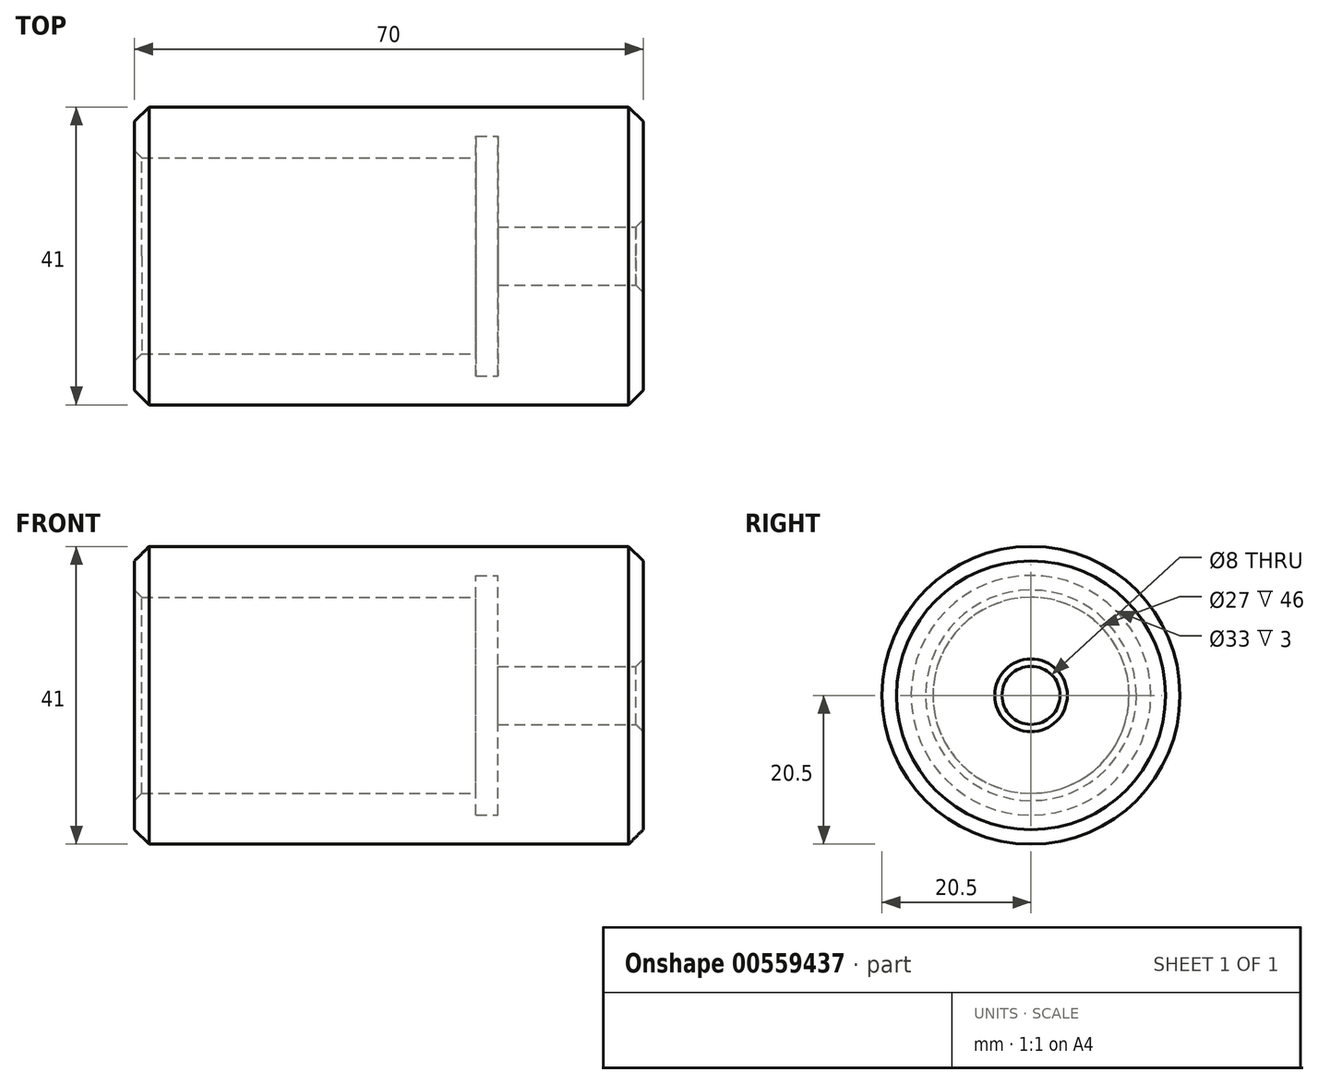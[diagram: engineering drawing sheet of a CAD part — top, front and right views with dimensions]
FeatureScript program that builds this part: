
annotation { "Feature Type Name" : "Feature", "Feature Type Description" : "" }
export const myFeature = defineFeature(function(context is Context, id is Id, definition is map)
    precondition{}
    {
        {
            var Q0;
            Q0=qCreatedBy(makeId("Front.planeOp"),FACE);
            var sketch = newSketch(context, id + "F0", { "sketchPlane" : qUnion([Q0])});
            skLineSegment(sketch, "E0", {"start": v(0, 4) * mm, "end": v(20, 4) * mm});
            skLineSegment(sketch, "E1", {"start": v(20, 4) * mm, "end": v(20, 20.5) * mm});
            skLineSegment(sketch, "E2", {"start": v(20, 20.5) * mm, "end": v(-50, 20.5) * mm});
            skLineSegment(sketch, "E3", {"start": v(-50, 20.5) * mm, "end": v(-50, 13.5) * mm});
            skLineSegment(sketch, "E4", {"start": v(-3, 13.5) * mm, "end": v(-50, 13.5) * mm});
            skLineSegment(sketch, "E5", {"start": v(0, 13.5) * mm, "end": v(0, 4) * mm});
            skPoint(sketch, "E6.start.orphan", {"position": v(-50, 0) * mm});
            skLineSegment(sketch, "E7", {"start": v(21.85, 0) * mm, "end": v(-52.14, 0) * mm, "construction": true});
            skLineSegment(sketch, "E8", {"start": v(-3, -1.98) * mm, "end": v(-3, 15.28) * mm, "construction": true});
            skLineSegment(sketch, "E9", {"start": v(-5.32, 16.5) * mm, "end": v(2.8, 16.5) * mm, "construction": true});
            skLineSegment(sketch, "E10", {"start": v(-3, 13.5) * mm, "end": v(-3, 16.5) * mm});
            skLineSegment(sketch, "E11", {"start": v(-3, 16.5) * mm, "end": v(0, 16.5) * mm});
            skLineSegment(sketch, "E12", {"start": v(0, 16.5) * mm, "end": v(0, 13.5) * mm});
            skSolve(sketch);
        }
        {
            var Q0;
            Q0=makeQuery(id+"F0.imprint","IMPRINT",FACE,{"disambiguationData":[TD([[makeQuery(id+"F0.imprint","IMPRINT",EDGE,{"derivedFrom":sQuery(id+"F0.wireOp",EDGE,"E0")}),1.0]])]});
            var Q1;
            Q1=sQuery(id+"F0.wireOp",EDGE,"E7");
            revolve(context, id + "F1", {"entities" : qUnion([Q0]), "axis" : qUnion([Q1]), "revolveType" : RevolveType.FULL});
        }
        {
            var Q0;
            Q0=makeQuery(id+"F1.opRevolve","SWEPT_EDGE",EDGE,{"disambiguationData":[OSD([sQuery(id+"F0.wireOp",EDGE,"E2"),sQuery(id+"F0.wireOp",EDGE,"E3")])]});
            var Q1;
            Q1=makeQuery(id+"F1.opRevolve","SWEPT_EDGE",EDGE,{"disambiguationData":[OSD([sQuery(id+"F0.wireOp",EDGE,"E1"),sQuery(id+"F0.wireOp",EDGE,"E2")])]});
            chamfer(context, id + "F2", {"entities" : qUnion([Q0, Q1]), "width" : 2 * mm, "tangentPropagation" : true});
        }
        {
            var Q0;
            Q0=makeQuery(id+"F1.opRevolve","SWEPT_EDGE",EDGE,{"disambiguationData":[OSD([sQuery(id+"F0.wireOp",EDGE,"E3"),sQuery(id+"F0.wireOp",EDGE,"E4")])]});
            var Q1;
            Q1=makeQuery(id+"F1.opRevolve","SWEPT_EDGE",EDGE,{"disambiguationData":[OSD([sQuery(id+"F0.wireOp",EDGE,"E0"),sQuery(id+"F0.wireOp",EDGE,"E1")])]});
            chamfer(context, id + "F3", {"entities" : qUnion([Q0, Q1]), "width" : 1 * mm, "tangentPropagation" : true});
        }
    });
